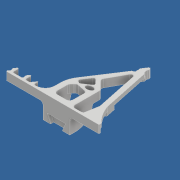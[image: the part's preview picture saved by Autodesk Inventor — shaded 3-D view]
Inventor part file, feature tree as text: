
AUTODESK INVENTOR PART (.ipt)
format: ipt  version: 2017 (Build 210142000, 142)  size: 1,384,448 bytes
history: native  units: mm
features: fillet x28, extrude x25, sketch x25, other x5, mirror x3, chamfer x1
ambient origin geometry x8: Origin, YZ Plane, XZ Plane, XY Plane, X Axis, Y Axis, Z Axis, Center Point
bodies: Body1 (feature_tree)
feature tree (87):
  other  "ソリッド1"
  extrude  "押し出し1"  Depth=100.0mm
  extrude  "押し出し2"  Depth=95.0mm
  extrude  "押し出し3"  Depth=20.0mm
  extrude  "押し出し4"  Depth=8.0mm
  other  "作業平面1"
  mirror  "ミラー1"
  extrude  "押し出し6"  Depth=10.0mm
  extrude  "押し出し7"  Depth=8.0mm
  extrude  "押し出し11"  Depth=8.0mm
  other  "iPad_mount_left"
  extrude  "押し出し14"  Depth=10.0mm TaperAngle=0.0deg
  extrude  "押し出し15"  Depth=40.0mm
  extrude  "押し出し16"  Depth=30.0mm
  extrude  "押し出し17"  Depth=4.0mm
  extrude  "押し出し18"  Depth=20.0mm TaperAngle=0.0deg
  extrude  "押し出し19"  Depth=7.5mm
  extrude  "押し出し20"  Depth=10.0mm
  extrude  "押し出し21"  Depth=15.0mm
  extrude  "押し出し22"  Depth=2.5mm
  extrude  "押し出し23"  Depth=20.0mm TaperAngle=0.0deg
  mirror  "ミラー2"
  extrude  "押し出し24"  Depth=25.0mm
  fillet  "フィレット39"  Radius=3.0mm
  fillet  "フィレット40"  [1 undecoded]
  fillet  "フィレット41"  Radius=10.0mm
  fillet  "フィレット42"  Radius=2.0mm
  fillet  "フィレット43"  Radius=10.0mm
  fillet  "フィレット44"  Radius=10.0mm
  fillet  "フィレット45"  Radius=10.0mm
  fillet  "フィレット46"  Radius=10.0mm
  fillet  "フィレット47"  Radius=2.0mm
  fillet  "フィレット48"  Radius=2.0mm
  fillet  "フィレット49"  Radius=2.0mm
  fillet  "フィレット52"  Radius=3.0mm
  fillet  "フィレット53"  Radius=2.0mm
  fillet  "フィレット54"  Radius=10.0mm
  fillet  "フィレット55"  Radius=5.0mm
  fillet  "フィレット56"  Radius=2.0mm
  fillet  "フィレット57"  Radius=2.0mm
  fillet  "フィレット58"  Radius=2.0mm
  fillet  "フィレット59"  Radius=2.0mm
  fillet  "フィレット60"  Radius=3.0mm
  fillet  "フィレット61"  Radius=7.0mm
  extrude  "押し出し25"  Depth=7.0mm TaperAngle=0.0deg
  extrude  "押し出し26"  Depth=7.0mm TaperAngle=0.0deg
  chamfer  "面取り1"  Distance=6.0mm
  fillet  "フィレット64"  Radius=5.0mm
  fillet  "フィレット65"  Radius=10.0mm
  fillet  "フィレット66"  Radius=9.424778mm
  other  "作業平面2"
  mirror  "ミラー3"
  extrude  "押し出し27"  Depth=12.0mm
  extrude  "押し出し28"  Depth=0.5mm
  extrude  "押し出し29"  Depth=1.5mm
  extrude  "押し出し30"  Depth=1.5mm
  fillet  "フィレット67"  Radius=1.0mm
  fillet  "フィレット68"  Radius=1.5mm
  fillet  "フィレット69"  Radius=2.5mm
  fillet  "フィレット70"  Radius=1.0mm
  extrude  "押し出し31"  Depth=1.0mm
  sketch  "スケッチ1"
  sketch  "スケッチ2"
  sketch  "スケッチ3"
  sketch  "スケッチ4"
  sketch  "スケッチ7"
  sketch  "スケッチ8"
  sketch  "スケッチ13"
  sketch  "スケッチ17"
  sketch  "スケッチ18"
  sketch  "スケッチ19"
  sketch  "スケッチ20"
  sketch  "スケッチ21"
  sketch  "スケッチ22"
  sketch  "スケッチ23"
  sketch  "スケッチ24"
  sketch  "スケッチ25"
  sketch  "スケッチ26"
  sketch  "スケッチ27"
  sketch  "スケッチ28"
  sketch  "スケッチ29"
  sketch  "スケッチ30"
  sketch  "スケッチ31"
  sketch  "スケッチ32"
  sketch  "スケッチ33"
  sketch  "スケッチ34"
  other  "メッシュ フィーチャ2"
note: 1 required parameter value undecoded (feature->parameter linkage not recoverable at this tier; creation-order binding heuristic only, values carry confidence <= 0.55)
